# Revit family: Toilet_Seat-Right_Width-American_Standard-5309110.020
name_source: partatom
category: Plumbing Fixtures
units: mm (PartAtom-declared; Revit-internal decimal feet)

## family parameters
Always vertical = No
Cut with Voids When Loaded = No
OmniClass Number = 23.45.05.21.11
OmniClass Title = Water Closets
Part Type = Normal
Room Calculation Point = No
Round Connector Dimension = Use Diameter
Shared = Yes
Work Plane-Based = Yes

## types (1)
- 5309110.020
    Assembly Code = D2010110
    CW Connection = No
    Cost = 0 $
    Default Elevation = 0"
    Description = Right Width Open Front Elongated Toilet Seat
    Finish = Polypropylene-American Standard-020-White
    HW Connection = No
    Installation Type = Toilet Mounted
    Manufacturer = American Standard
    Material = Polypropylene-American Standard-020-White
    Model = 5309110.020
    Product Documentation Link = https://americanstandard.box.com
    Product Page URL = https://www.americanstandard-us.com
    Revised Date = 03/01/2023
    URL = https://www.americanstandard-us.com
    Vent Connection = No
    Waste Connection = No
    Width = 16 7/16"

## geometry (parser evidence)
native form markers: Sweep x3
no freeform markers — native parametric forms only
